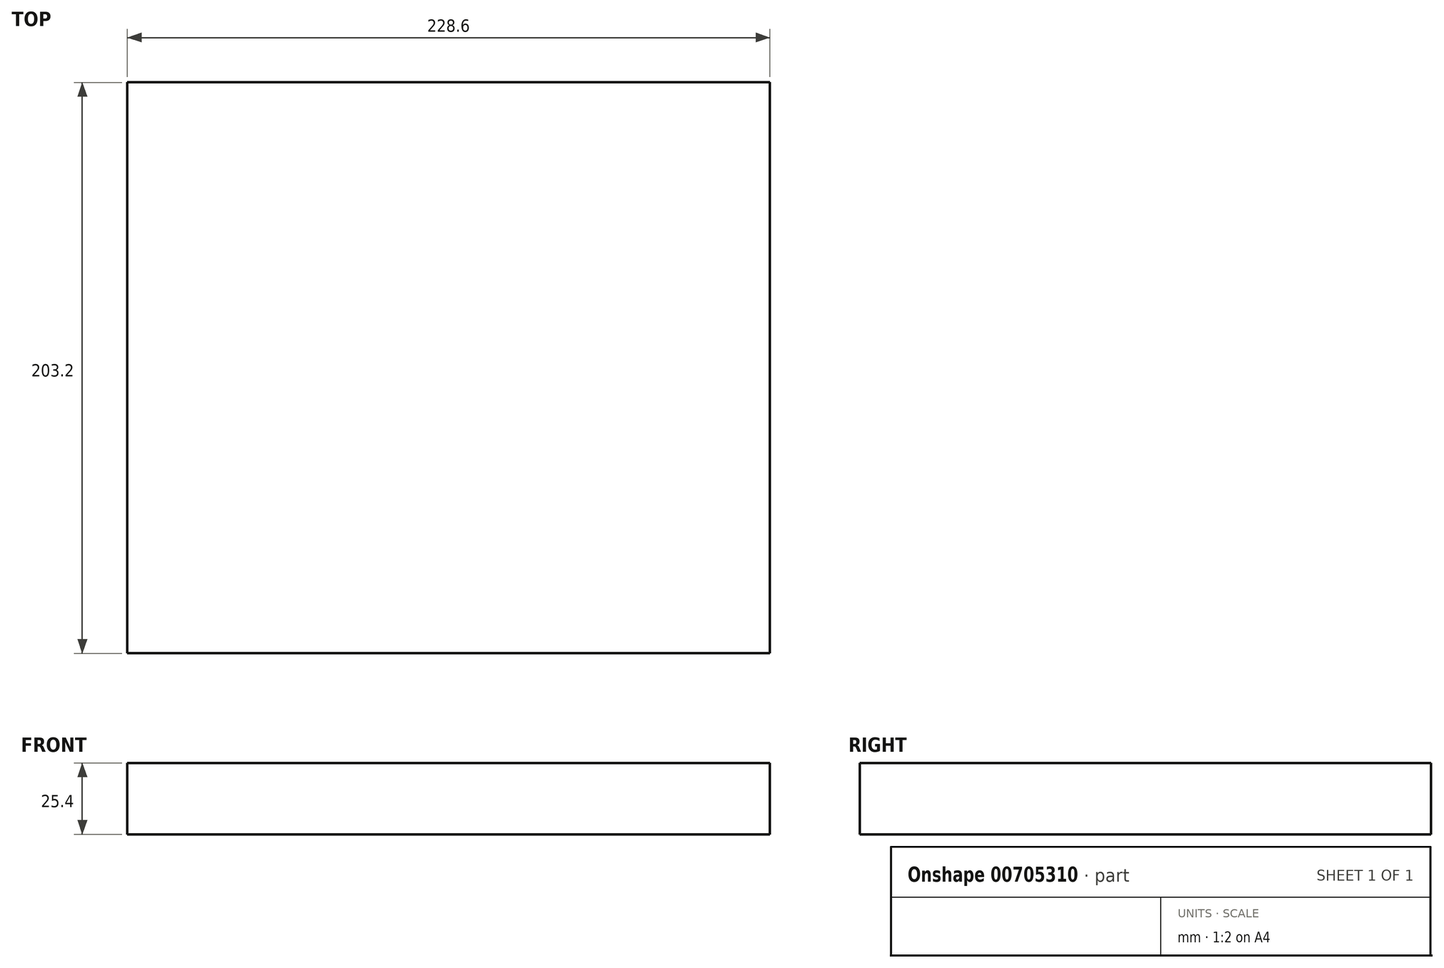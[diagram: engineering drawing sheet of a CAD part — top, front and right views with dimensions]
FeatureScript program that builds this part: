
annotation { "Feature Type Name" : "Feature", "Feature Type Description" : "" }
export const myFeature = defineFeature(function(context is Context, id is Id, definition is map)
    precondition{}
    {
        {
            var Q0;
            Q0=qCreatedBy(makeId("Top.planeOp"),FACE);
            var sketch = newSketch(context, id + "F0", { "sketchPlane" : qUnion([Q0])});
            skLineSegment(sketch, "E0.bottom", {"start": v(-109.51, 149.21) * mm, "end": v(119.09, 149.21) * mm});
            skLineSegment(sketch, "E0.top", {"start": v(-109.51, -53.99) * mm, "end": v(119.09, -53.99) * mm});
            skLineSegment(sketch, "E0.left", {"start": v(-109.51, 149.21) * mm, "end": v(-109.51, -53.99) * mm});
            skLineSegment(sketch, "E0.right", {"start": v(119.09, 149.21) * mm, "end": v(119.09, -53.99) * mm});
            skSolve(sketch);
        }
        {
            var Q0;
            Q0=makeQuery(id+"F0.imprint","IMPRINT",FACE,{"disambiguationData":[TD([[makeQuery(id+"F0.imprint","IMPRINT",EDGE,{"derivedFrom":sQuery(id+"F0.wireOp",EDGE,"E0.bottom")}),-1.0]])]});
            extrude(context, id + "F1", {"entities" : qUnion([Q0]), "depth" : 25.4 * mm, "offsetDistance" : 25.4 * mm});
        }
    });
